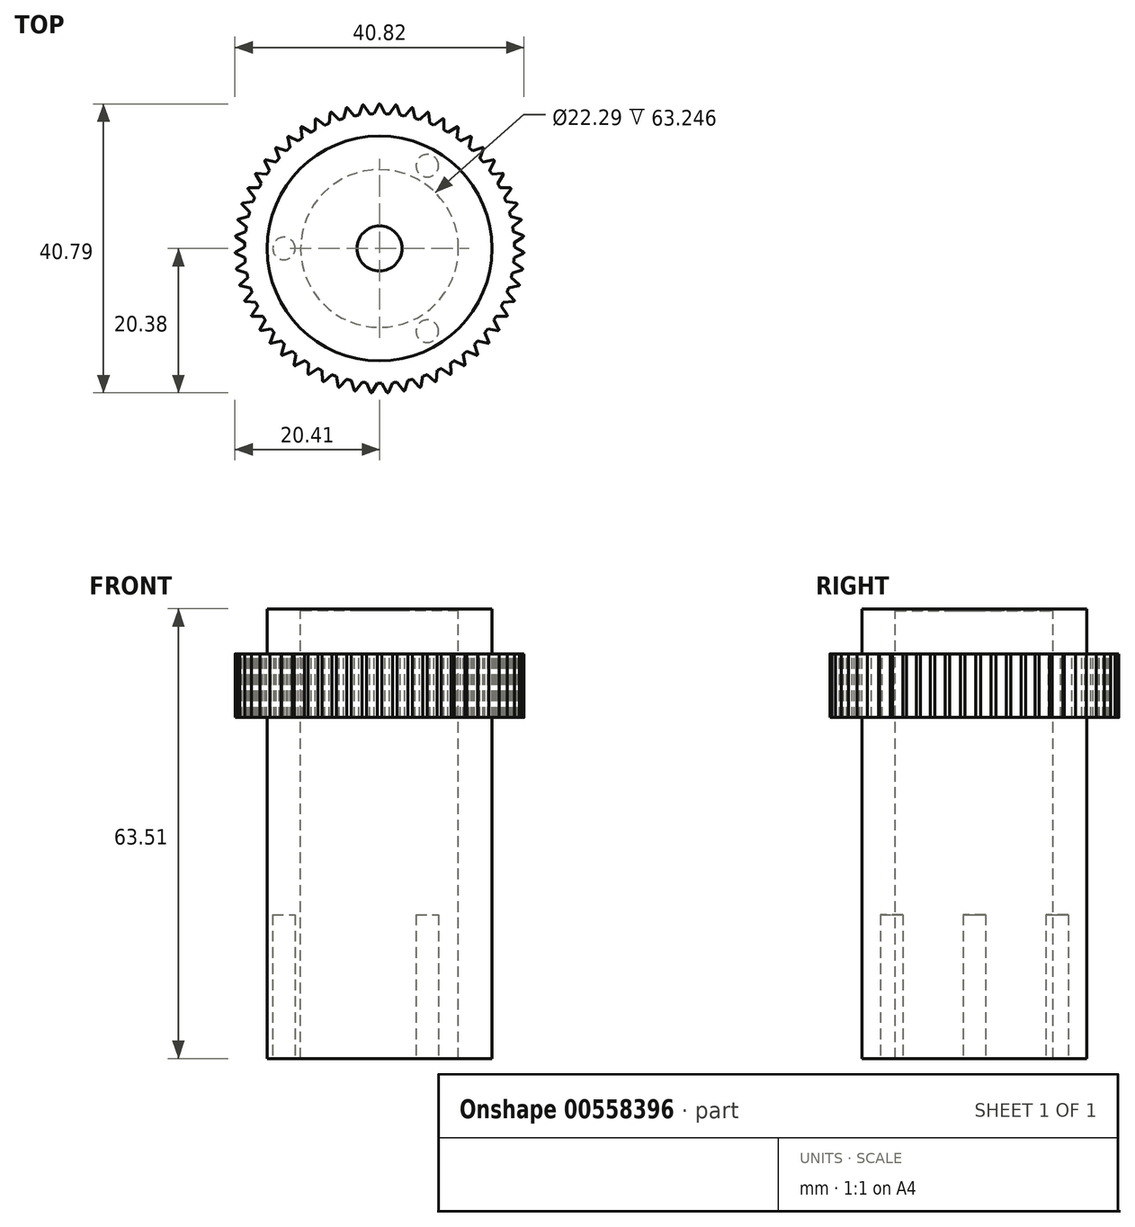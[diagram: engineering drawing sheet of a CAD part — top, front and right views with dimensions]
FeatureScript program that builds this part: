
annotation { "Feature Type Name" : "Feature", "Feature Type Description" : "" }
export const myFeature = defineFeature(function(context is Context, id is Id, definition is map)
    precondition{}
    {
        {
            var Q0;
            Q0=qCreatedBy(makeId("Front.planeOp"),FACE);
            var sketch = newSketch(context, id + "F0", { "sketchPlane" : qUnion([Q0])});
            skLineSegment(sketch, "E0.bottom", {"start": v(11.15, 34.92) * mm, "end": v(15.88, 34.92) * mm});
            skLineSegment(sketch, "E0.top", {"start": v(11.15, -28.58) * mm, "end": v(15.88, -28.58) * mm});
            skLineSegment(sketch, "E0.left", {"start": v(11.15, 34.92) * mm, "end": v(11.15, -28.58) * mm});
            skLineSegment(sketch, "E0.right", {"start": v(15.88, 34.92) * mm, "end": v(15.88, -28.58) * mm});
            skLineSegment(sketch, "E1", {"start": v(0, 43.43) * mm, "end": v(0, -51.55) * mm, "construction": true});
            skSolve(sketch);
        }
        {
            var Q0;
            Q0 = qSketchRegion(id + "F0", true);
            var Q1;
            Q1=sQuery(id+"F0.wireOp",EDGE,"E1");
            revolve(context, id + "F1", {"entities" : qUnion([Q0]), "axis" : qUnion([Q1]), "revolveType" : RevolveType.FULL});
        }
        {
            var Q0;
            Q0=makeQuery(id+"F1.opRevolve","SWEPT_FACE",FACE,{"disambiguationData":[OSD([sQuery(id+"F0.wireOp",EDGE,"E0.top")])]});
            var sketch = newSketch(context, id + "F2", { "sketchPlane" : qUnion([Q0])});
            skCircle(sketch, "E2", {"center": v(6.75, 11.69) * mm, "radius": 1.59 * mm});
            skCircle(sketch, "E3", {"center": v(6.75, -11.69) * mm, "radius": 1.59 * mm});
            skCircle(sketch, "E4", {"center": v(-13.5, 0) * mm, "radius": 1.59 * mm});
            skCircle(sketch, "E5", {"center": v(0, 0) * mm, "radius": 13.5 * mm});
            skLineSegment(sketch, "E6", {"start": v(0, 0) * mm, "end": v(-29.1, 0) * mm, "construction": true});
            skLineSegment(sketch, "E7", {"start": v(0, 0) * mm, "end": v(10.24, 17.73) * mm, "construction": true});
            skLineSegment(sketch, "E8", {"start": v(0, 0) * mm, "end": v(11.33, -19.63) * mm, "construction": true});
            skSolve(sketch);
        }
        {
            var Q0;
            {var subQ0=sQuery(id+"F2.wireOp",EDGE,"E5");var subQ1=sQuery(id+"F2.wireOp",EDGE,"E3");var subQ2=makeQuery(id+"F2.imprint","INTERSECT",VERTEX,{"disambiguationData":[OD(0.0)],"derivedFrom":[subQ1,subQ0]});Q0=makeQuery(id+"F2.imprint","IMPRINT",FACE,{"disambiguationData":[TD([[makeQuery(id+"F2.imprint","IMPRINT",EDGE,{"disambiguationData":[TD([[subQ2,-1.0]])],"derivedFrom":subQ1}),1.0]])]});}
            var Q1;
            {var subQ0=sQuery(id+"F2.wireOp",EDGE,"E5");var subQ1=sQuery(id+"F2.wireOp",EDGE,"E3");var subQ2=makeQuery(id+"F2.imprint","INTERSECT",VERTEX,{"disambiguationData":[OD(0.0)],"derivedFrom":[subQ1,subQ0]});Q1=makeQuery(id+"F2.imprint","IMPRINT",FACE,{"disambiguationData":[TD([[makeQuery(id+"F2.imprint","IMPRINT",EDGE,{"disambiguationData":[TD([[subQ2,1.0]])],"derivedFrom":subQ1}),1.0]])]});}
            var Q2;
            {var subQ0=sQuery(id+"F2.wireOp",EDGE,"E5");var subQ1=sQuery(id+"F2.wireOp",EDGE,"E2");var subQ2=makeQuery(id+"F2.imprint","INTERSECT",VERTEX,{"disambiguationData":[OD(0.0)],"derivedFrom":[subQ1,subQ0]});Q2=makeQuery(id+"F2.imprint","IMPRINT",FACE,{"disambiguationData":[TD([[makeQuery(id+"F2.imprint","IMPRINT",EDGE,{"disambiguationData":[TD([[subQ2,-1.0]])],"derivedFrom":subQ1}),1.0]])]});}
            var Q3;
            {var subQ0=sQuery(id+"F2.wireOp",EDGE,"E5");var subQ1=sQuery(id+"F2.wireOp",EDGE,"E2");var subQ2=makeQuery(id+"F2.imprint","INTERSECT",VERTEX,{"disambiguationData":[OD(0.0)],"derivedFrom":[subQ1,subQ0]});Q3=makeQuery(id+"F2.imprint","IMPRINT",FACE,{"disambiguationData":[TD([[makeQuery(id+"F2.imprint","IMPRINT",EDGE,{"disambiguationData":[TD([[subQ2,1.0]])],"derivedFrom":subQ1}),1.0]])]});}
            var Q4;
            {var subQ0=sQuery(id+"F2.wireOp",EDGE,"E5");var subQ1=sQuery(id+"F2.wireOp",EDGE,"E4");var subQ2=makeQuery(id+"F2.imprint","INTERSECT",VERTEX,{"disambiguationData":[OD(0.0)],"derivedFrom":[subQ1,subQ0]});Q4=makeQuery(id+"F2.imprint","IMPRINT",FACE,{"disambiguationData":[TD([[makeQuery(id+"F2.imprint","IMPRINT",EDGE,{"disambiguationData":[TD([[subQ2,-1.0]])],"derivedFrom":subQ1}),1.0]])]});}
            var Q5;
            {var subQ0=sQuery(id+"F2.wireOp",EDGE,"E5");var subQ1=sQuery(id+"F2.wireOp",EDGE,"E4");var subQ2=makeQuery(id+"F2.imprint","INTERSECT",VERTEX,{"disambiguationData":[OD(0.0)],"derivedFrom":[subQ1,subQ0]});Q5=makeQuery(id+"F2.imprint","IMPRINT",FACE,{"disambiguationData":[TD([[makeQuery(id+"F2.imprint","IMPRINT",EDGE,{"disambiguationData":[TD([[subQ2,1.0]])],"derivedFrom":subQ1}),1.0]])]});}
            extrude(context, id + "F3", {"entities" : qUnion([Q0, Q1, Q2, Q3, Q4, Q5]), "operationType" : NewBodyOperationType.REMOVE, "oppositeDirection" : true, "depth" : 20.32 * mm, "offsetDistance" : 25.4 * mm});
        }
        {
            var Q0;
            Q0=makeQuery(id+"F1.opRevolve","SWEPT_FACE",FACE,{"disambiguationData":[OSD([sQuery(id+"F0.wireOp",EDGE,"E0.bottom")])]});
            var sketch = newSketch(context, id + "F4", { "sketchPlane" : qUnion([Q0])});
            skCircle(sketch, "E9", {"center": v(0, 0) * mm, "radius": 3.18 * mm});
            skSolve(sketch);
        }
        {
            var Q0;
            Q0=makeQuery(id+"F4.imprint","IMPRINT",FACE,{"disambiguationData":[TD([[makeQuery(id+"F4.imprint","IMPRINT",EDGE,{"derivedFrom":sQuery(id+"F4.wireOp",EDGE,"E9")}),-1.0]])]});
            extrude(context, id + "F5", {"entities" : qUnion([Q0]), "operationType" : NewBodyOperationType.ADD, "oppositeDirection" : true, "depth" : 0.25 * mm, "offsetDistance" : 25.4 * mm});
        }
        {
            var Q0;
            {var subQ0=sQuery(id+"F0.wireOp",EDGE,"E0.bottom");Q0=makeQuery(id+"F5.boolean.opBoolean","MERGE",FACE,{"derivedFrom":[makeQuery(id+"F1.opRevolve","SWEPT_FACE",FACE,{"disambiguationData":[OSD([subQ0])]}),makeQuery(id+"F5.opExtrude","CAP_FACE",FACE,{"disambiguationData":[OSD([subQ0,sQuery(id+"F0.wireOp",EDGE,"E0.left"),sQuery(id+"F4.wireOp",EDGE,"E9")])],"isStart":true})]});}
            cPlane(context, id + "F6", {"entities" : qUnion([Q0]), "cplaneType" : CPlaneType.OFFSET, "offset" : 6.35 * mm, "oppositeDirection" : true, "width" : 152.4 * mm, "height" : 152.4 * mm});
        }
        {
            var Q0;
            Q0=qCreatedBy(id+"F6.planeOp",FACE);
            var sketch = newSketch(context, id + "F7", { "sketchPlane" : qUnion([Q0])});
            skCircle(sketch, "E10", {"center": v(0, 0) * mm, "radius": 19.05 * mm});
            skLineSegment(sketch, "E11", {"start": v(-0.76, 19.03) * mm, "end": v(-0.11, 20.34) * mm});
            skLineSegment(sketch, "E12", {"start": v(0.11, 20.34) * mm, "end": v(0.76, 19.03) * mm});
            skPoint(sketch, "E13.visualSharp", {"position": v(0, 20.57) * mm});
            skArc(sketch, "E14.filletArc", {"start": v(0.11, 20.34) * mm, "mid": v(0, 20.41) * mm, "end": v(-0.11, 20.34) * mm});
            skLineSegment(sketch, "E15.1.0", {"start": v(-2.2, 20.22) * mm, "end": v(-1.41, 19) * mm});
            skLineSegment(sketch, "E15.1.1", {"start": v(-2.93, 18.82) * mm, "end": v(-2.43, 20.2) * mm});
            skArc(sketch, "E15.1.2", {"start": v(-2.2, 20.22) * mm, "mid": v(-2.33, 20.28) * mm, "end": v(-2.43, 20.2) * mm});
            skLineSegment(sketch, "E15.2.0", {"start": v(-4.5, 19.84) * mm, "end": v(-3.57, 18.71) * mm});
            skLineSegment(sketch, "E15.2.1", {"start": v(-5.05, 18.37) * mm, "end": v(-4.72, 19.79) * mm});
            skArc(sketch, "E15.2.2", {"start": v(-4.5, 19.84) * mm, "mid": v(-4.62, 19.88) * mm, "end": v(-4.72, 19.79) * mm});
            skLineSegment(sketch, "E15.3.0", {"start": v(-6.73, 19.2) * mm, "end": v(-5.68, 18.18) * mm});
            skLineSegment(sketch, "E15.3.1", {"start": v(-7.11, 17.67) * mm, "end": v(-6.94, 19.12) * mm});
            skArc(sketch, "E15.3.2", {"start": v(-6.73, 19.2) * mm, "mid": v(-6.86, 19.23) * mm, "end": v(-6.94, 19.12) * mm});
            skLineSegment(sketch, "E15.4.0", {"start": v(-8.87, 18.3) * mm, "end": v(-7.71, 17.42) * mm});
            skLineSegment(sketch, "E15.4.1", {"start": v(-9.08, 16.75) * mm, "end": v(-9.08, 18.2) * mm});
            skArc(sketch, "E15.4.2", {"start": v(-8.87, 18.3) * mm, "mid": v(-9, 18.32) * mm, "end": v(-9.08, 18.2) * mm});
            skLineSegment(sketch, "E15.5.0", {"start": v(-10.9, 17.18) * mm, "end": v(-9.65, 16.43) * mm});
            skLineSegment(sketch, "E15.5.1", {"start": v(-10.93, 15.6) * mm, "end": v(-11.1, 17.05) * mm});
            skArc(sketch, "E15.5.2", {"start": v(-10.9, 17.18) * mm, "mid": v(-11.04, 17.17) * mm, "end": v(-11.1, 17.05) * mm});
            skLineSegment(sketch, "E15.6.0", {"start": v(-12.79, 15.82) * mm, "end": v(-11.46, 15.22) * mm});
            skLineSegment(sketch, "E15.6.1", {"start": v(-12.64, 14.25) * mm, "end": v(-12.97, 15.68) * mm});
            skArc(sketch, "E15.6.2", {"start": v(-12.79, 15.82) * mm, "mid": v(-12.92, 15.8) * mm, "end": v(-12.97, 15.68) * mm});
            skLineSegment(sketch, "E15.7.0", {"start": v(-14.51, 14.26) * mm, "end": v(-13.12, 13.81) * mm});
            skLineSegment(sketch, "E15.7.1", {"start": v(-14.18, 12.72) * mm, "end": v(-14.67, 14.1) * mm});
            skArc(sketch, "E15.7.2", {"start": v(-14.51, 14.26) * mm, "mid": v(-14.64, 14.23) * mm, "end": v(-14.67, 14.1) * mm});
            skLineSegment(sketch, "E15.8.0", {"start": v(-16.04, 12.51) * mm, "end": v(-14.6, 12.23) * mm});
            skLineSegment(sketch, "E15.8.1", {"start": v(-15.54, 11.02) * mm, "end": v(-16.18, 12.33) * mm});
            skArc(sketch, "E15.8.2", {"start": v(-16.04, 12.51) * mm, "mid": v(-16.17, 12.47) * mm, "end": v(-16.18, 12.33) * mm});
            skLineSegment(sketch, "E15.9.0", {"start": v(-17.36, 10.6) * mm, "end": v(-15.9, 10.48) * mm});
            skLineSegment(sketch, "E15.9.1", {"start": v(-16.7, 9.18) * mm, "end": v(-17.48, 10.4) * mm});
            skArc(sketch, "E15.9.2", {"start": v(-17.36, 10.6) * mm, "mid": v(-17.48, 10.54) * mm, "end": v(-17.48, 10.4) * mm});
            skLineSegment(sketch, "E15.10.0", {"start": v(-18.46, 8.55) * mm, "end": v(-17, 8.6) * mm});
            skLineSegment(sketch, "E15.10.1", {"start": v(-17.63, 7.21) * mm, "end": v(-18.55, 8.35) * mm});
            skArc(sketch, "E15.10.2", {"start": v(-18.46, 8.55) * mm, "mid": v(-18.57, 8.48) * mm, "end": v(-18.55, 8.35) * mm});
            skLineSegment(sketch, "E15.11.0", {"start": v(-19.31, 6.4) * mm, "end": v(-17.87, 6.6) * mm});
            skLineSegment(sketch, "E15.11.1", {"start": v(-18.34, 5.16) * mm, "end": v(-19.38, 6.18) * mm});
            skArc(sketch, "E15.11.2", {"start": v(-19.31, 6.4) * mm, "mid": v(-19.42, 6.3) * mm, "end": v(-19.38, 6.18) * mm});
            skLineSegment(sketch, "E15.12.0", {"start": v(-19.92, 4.15) * mm, "end": v(-18.5, 4.53) * mm});
            skLineSegment(sketch, "E15.12.1", {"start": v(-18.8, 3.03) * mm, "end": v(-19.96, 3.93) * mm});
            skArc(sketch, "E15.12.2", {"start": v(-19.92, 4.15) * mm, "mid": v(-20, 4.05) * mm, "end": v(-19.96, 3.93) * mm});
            skLineSegment(sketch, "E15.13.0", {"start": v(-20.26, 1.85) * mm, "end": v(-18.9, 2.39) * mm});
            skLineSegment(sketch, "E15.13.1", {"start": v(-19.03, 0.87) * mm, "end": v(-20.28, 1.63) * mm});
            skArc(sketch, "E15.13.2", {"start": v(-20.26, 1.85) * mm, "mid": v(-20.34, 1.75) * mm, "end": v(-20.28, 1.63) * mm});
            skLineSegment(sketch, "E15.14.0", {"start": v(-20.34, -0.47) * mm, "end": v(-19.05, 0.22) * mm});
            skLineSegment(sketch, "E15.14.1", {"start": v(-19, -1.3) * mm, "end": v(-20.33, -0.7) * mm});
            skArc(sketch, "E15.14.2", {"start": v(-20.34, -0.47) * mm, "mid": v(-20.4, -0.58) * mm, "end": v(-20.33, -0.7) * mm});
            skLineSegment(sketch, "E15.15.0", {"start": v(-20.15, -2.78) * mm, "end": v(-18.95, -1.95) * mm});
            skLineSegment(sketch, "E15.15.1", {"start": v(-18.73, -3.46) * mm, "end": v(-20.12, -3) * mm});
            skArc(sketch, "E15.15.2", {"start": v(-20.15, -2.78) * mm, "mid": v(-20.2, -2.9) * mm, "end": v(-20.12, -3) * mm});
            skLineSegment(sketch, "E15.16.0", {"start": v(-19.7, -5.06) * mm, "end": v(-18.6, -4.1) * mm});
            skLineSegment(sketch, "E15.16.1", {"start": v(-18.22, -5.58) * mm, "end": v(-19.65, -5.28) * mm});
            skArc(sketch, "E15.16.2", {"start": v(-19.7, -5.06) * mm, "mid": v(-19.74, -5.19) * mm, "end": v(-19.65, -5.28) * mm});
            skLineSegment(sketch, "E15.17.0", {"start": v(-19, -7.27) * mm, "end": v(-18.01, -6.2) * mm});
            skLineSegment(sketch, "E15.17.1", {"start": v(-17.46, -7.62) * mm, "end": v(-18.92, -7.49) * mm});
            skArc(sketch, "E15.17.2", {"start": v(-19, -7.27) * mm, "mid": v(-19.02, -7.4) * mm, "end": v(-18.92, -7.49) * mm});
            skLineSegment(sketch, "E15.18.0", {"start": v(-18.05, -9.4) * mm, "end": v(-17.2, -8.2) * mm});
            skLineSegment(sketch, "E15.18.1", {"start": v(-16.48, -9.56) * mm, "end": v(-17.94, -9.6) * mm});
            skArc(sketch, "E15.18.2", {"start": v(-18.05, -9.4) * mm, "mid": v(-18.06, -9.53) * mm, "end": v(-17.94, -9.6) * mm});
            skLineSegment(sketch, "E15.19.0", {"start": v(-16.86, -11.39) * mm, "end": v(-16.14, -10.12) * mm});
            skLineSegment(sketch, "E15.19.1", {"start": v(-15.28, -11.37) * mm, "end": v(-16.73, -11.58) * mm});
            skArc(sketch, "E15.19.2", {"start": v(-16.86, -11.39) * mm, "mid": v(-16.85, -11.52) * mm, "end": v(-16.73, -11.58) * mm});
            skLineSegment(sketch, "E15.20.0", {"start": v(-15.45, -13.24) * mm, "end": v(-14.88, -11.89) * mm});
            skLineSegment(sketch, "E15.20.1", {"start": v(-13.89, -13.04) * mm, "end": v(-15.3, -13.4) * mm});
            skArc(sketch, "E15.20.2", {"start": v(-15.45, -13.24) * mm, "mid": v(-15.43, -13.37) * mm, "end": v(-15.3, -13.4) * mm});
            skLineSegment(sketch, "E15.21.0", {"start": v(-13.84, -14.91) * mm, "end": v(-13.43, -13.5) * mm});
            skLineSegment(sketch, "E15.21.1", {"start": v(-12.3, -14.54) * mm, "end": v(-13.67, -15.07) * mm});
            skArc(sketch, "E15.21.2", {"start": v(-13.84, -14.91) * mm, "mid": v(-13.8, -15.04) * mm, "end": v(-13.67, -15.07) * mm});
            skLineSegment(sketch, "E15.22.0", {"start": v(-12.05, -16.4) * mm, "end": v(-11.8, -14.95) * mm});
            skLineSegment(sketch, "E15.22.1", {"start": v(-10.57, -15.85) * mm, "end": v(-11.87, -16.53) * mm});
            skArc(sketch, "E15.22.2", {"start": v(-12.05, -16.4) * mm, "mid": v(-12, -16.52) * mm, "end": v(-11.87, -16.53) * mm});
            skLineSegment(sketch, "E15.23.0", {"start": v(-10.1, -17.66) * mm, "end": v(-10.02, -16.2) * mm});
            skLineSegment(sketch, "E15.23.1", {"start": v(-8.7, -16.95) * mm, "end": v(-9.9, -17.77) * mm});
            skArc(sketch, "E15.23.2", {"start": v(-10.1, -17.66) * mm, "mid": v(-10.04, -17.78) * mm, "end": v(-9.9, -17.77) * mm});
            skLineSegment(sketch, "E15.24.0", {"start": v(-8.02, -18.7) * mm, "end": v(-8.11, -17.24) * mm});
            skLineSegment(sketch, "E15.24.1", {"start": v(-6.7, -17.83) * mm, "end": v(-7.81, -18.78) * mm});
            skArc(sketch, "E15.24.2", {"start": v(-8.02, -18.7) * mm, "mid": v(-7.95, -18.8) * mm, "end": v(-7.81, -18.78) * mm});
            skLineSegment(sketch, "E15.25.0", {"start": v(-5.84, -19.49) * mm, "end": v(-6.1, -18.05) * mm});
            skLineSegment(sketch, "E15.25.1", {"start": v(-4.63, -18.48) * mm, "end": v(-5.62, -19.55) * mm});
            skArc(sketch, "E15.25.2", {"start": v(-5.84, -19.49) * mm, "mid": v(-5.75, -19.59) * mm, "end": v(-5.62, -19.55) * mm});
            skLineSegment(sketch, "E15.26.0", {"start": v(-3.58, -20.03) * mm, "end": v(-4, -18.63) * mm});
            skLineSegment(sketch, "E15.26.1", {"start": v(-2.5, -18.89) * mm, "end": v(-3.36, -20.07) * mm});
            skArc(sketch, "E15.26.2", {"start": v(-3.58, -20.03) * mm, "mid": v(-3.48, -20.12) * mm, "end": v(-3.36, -20.07) * mm});
            skLineSegment(sketch, "E15.27.0", {"start": v(-1.28, -20.3) * mm, "end": v(-1.85, -18.96) * mm});
            skLineSegment(sketch, "E15.27.1", {"start": v(-0.33, -19.05) * mm, "end": v(-1.05, -20.32) * mm});
            skArc(sketch, "E15.27.2", {"start": v(-1.28, -20.3) * mm, "mid": v(-1.17, -20.38) * mm, "end": v(-1.05, -20.32) * mm});
            skLineSegment(sketch, "E15.28.0", {"start": v(1.05, -20.32) * mm, "end": v(0.33, -19.05) * mm});
            skLineSegment(sketch, "E15.28.1", {"start": v(1.85, -18.96) * mm, "end": v(1.28, -20.3) * mm});
            skArc(sketch, "E15.28.2", {"start": v(1.05, -20.32) * mm, "mid": v(1.17, -20.38) * mm, "end": v(1.28, -20.3) * mm});
            skLineSegment(sketch, "E15.29.0", {"start": v(3.36, -20.07) * mm, "end": v(2.5, -18.89) * mm});
            skLineSegment(sketch, "E15.29.1", {"start": v(4, -18.63) * mm, "end": v(3.58, -20.03) * mm});
            skArc(sketch, "E15.29.2", {"start": v(3.36, -20.07) * mm, "mid": v(3.48, -20.12) * mm, "end": v(3.58, -20.03) * mm});
            skLineSegment(sketch, "E16.3.30.0", {"start": v(6.1, -18.05) * mm, "end": v(5.84, -19.49) * mm});
            skLineSegment(sketch, "E16.5.30.0", {"start": v(5.62, -19.55) * mm, "end": v(4.63, -18.48) * mm});
            skArc(sketch, "E16.6.30.0", {"start": v(5.62, -19.55) * mm, "mid": v(5.75, -19.59) * mm, "end": v(5.84, -19.49) * mm});
            skLineSegment(sketch, "E16.3.31.0", {"start": v(8.11, -17.24) * mm, "end": v(8.02, -18.7) * mm});
            skLineSegment(sketch, "E16.5.31.0", {"start": v(7.81, -18.78) * mm, "end": v(6.7, -17.83) * mm});
            skArc(sketch, "E16.6.31.0", {"start": v(7.81, -18.78) * mm, "mid": v(7.95, -18.8) * mm, "end": v(8.02, -18.7) * mm});
            skLineSegment(sketch, "E16.3.32.0", {"start": v(10.02, -16.2) * mm, "end": v(10.1, -17.66) * mm});
            skLineSegment(sketch, "E16.5.32.0", {"start": v(9.9, -17.77) * mm, "end": v(8.7, -16.95) * mm});
            skArc(sketch, "E16.6.32.0", {"start": v(9.9, -17.77) * mm, "mid": v(10.04, -17.78) * mm, "end": v(10.1, -17.66) * mm});
            skLineSegment(sketch, "E16.3.33.0", {"start": v(11.8, -14.95) * mm, "end": v(12.05, -16.4) * mm});
            skLineSegment(sketch, "E16.5.33.0", {"start": v(11.87, -16.53) * mm, "end": v(10.57, -15.85) * mm});
            skArc(sketch, "E16.6.33.0", {"start": v(11.87, -16.53) * mm, "mid": v(12, -16.52) * mm, "end": v(12.05, -16.4) * mm});
            skLineSegment(sketch, "E16.3.34.0", {"start": v(13.43, -13.5) * mm, "end": v(13.84, -14.91) * mm});
            skLineSegment(sketch, "E16.5.34.0", {"start": v(13.67, -15.07) * mm, "end": v(12.3, -14.54) * mm});
            skArc(sketch, "E16.6.34.0", {"start": v(13.67, -15.07) * mm, "mid": v(13.8, -15.04) * mm, "end": v(13.84, -14.91) * mm});
            skLineSegment(sketch, "E16.3.35.0", {"start": v(14.88, -11.89) * mm, "end": v(15.45, -13.24) * mm});
            skLineSegment(sketch, "E16.5.35.0", {"start": v(15.3, -13.4) * mm, "end": v(13.89, -13.04) * mm});
            skArc(sketch, "E16.6.35.0", {"start": v(15.3, -13.4) * mm, "mid": v(15.43, -13.37) * mm, "end": v(15.45, -13.24) * mm});
            skLineSegment(sketch, "E16.3.36.0", {"start": v(16.14, -10.12) * mm, "end": v(16.86, -11.39) * mm});
            skLineSegment(sketch, "E16.5.36.0", {"start": v(16.73, -11.58) * mm, "end": v(15.28, -11.37) * mm});
            skArc(sketch, "E16.6.36.0", {"start": v(16.73, -11.58) * mm, "mid": v(16.85, -11.52) * mm, "end": v(16.86, -11.39) * mm});
            skLineSegment(sketch, "E16.3.37.0", {"start": v(17.2, -8.2) * mm, "end": v(18.05, -9.4) * mm});
            skLineSegment(sketch, "E16.5.37.0", {"start": v(17.94, -9.6) * mm, "end": v(16.48, -9.56) * mm});
            skArc(sketch, "E16.6.37.0", {"start": v(17.94, -9.6) * mm, "mid": v(18.06, -9.53) * mm, "end": v(18.05, -9.4) * mm});
            skLineSegment(sketch, "E16.3.38.0", {"start": v(18.01, -6.2) * mm, "end": v(19, -7.27) * mm});
            skLineSegment(sketch, "E16.5.38.0", {"start": v(18.92, -7.49) * mm, "end": v(17.46, -7.62) * mm});
            skArc(sketch, "E16.6.38.0", {"start": v(18.92, -7.49) * mm, "mid": v(19.02, -7.4) * mm, "end": v(19, -7.27) * mm});
            skLineSegment(sketch, "E16.3.39.0", {"start": v(18.6, -4.1) * mm, "end": v(19.7, -5.06) * mm});
            skLineSegment(sketch, "E16.5.39.0", {"start": v(19.65, -5.28) * mm, "end": v(18.22, -5.58) * mm});
            skArc(sketch, "E16.6.39.0", {"start": v(19.65, -5.28) * mm, "mid": v(19.74, -5.19) * mm, "end": v(19.7, -5.06) * mm});
            skLineSegment(sketch, "E16.3.40.0", {"start": v(18.95, -1.95) * mm, "end": v(20.15, -2.78) * mm});
            skLineSegment(sketch, "E16.5.40.0", {"start": v(20.12, -3) * mm, "end": v(18.73, -3.46) * mm});
            skArc(sketch, "E16.6.40.0", {"start": v(20.12, -3) * mm, "mid": v(20.2, -2.9) * mm, "end": v(20.15, -2.78) * mm});
            skLineSegment(sketch, "E16.3.41.0", {"start": v(19.05, 0.22) * mm, "end": v(20.34, -0.47) * mm});
            skLineSegment(sketch, "E16.5.41.0", {"start": v(20.33, -0.7) * mm, "end": v(19, -1.3) * mm});
            skArc(sketch, "E16.6.41.0", {"start": v(20.33, -0.7) * mm, "mid": v(20.4, -0.58) * mm, "end": v(20.34, -0.47) * mm});
            skLineSegment(sketch, "E16.3.42.0", {"start": v(18.9, 2.39) * mm, "end": v(20.26, 1.85) * mm});
            skLineSegment(sketch, "E16.5.42.0", {"start": v(20.28, 1.63) * mm, "end": v(19.03, 0.87) * mm});
            skArc(sketch, "E16.6.42.0", {"start": v(20.28, 1.63) * mm, "mid": v(20.34, 1.75) * mm, "end": v(20.26, 1.85) * mm});
            skLineSegment(sketch, "E16.3.43.0", {"start": v(18.5, 4.53) * mm, "end": v(19.92, 4.15) * mm});
            skLineSegment(sketch, "E16.5.43.0", {"start": v(19.96, 3.93) * mm, "end": v(18.8, 3.03) * mm});
            skArc(sketch, "E16.6.43.0", {"start": v(19.96, 3.93) * mm, "mid": v(20, 4.05) * mm, "end": v(19.92, 4.15) * mm});
            skLineSegment(sketch, "E16.3.44.0", {"start": v(17.87, 6.6) * mm, "end": v(19.31, 6.4) * mm});
            skLineSegment(sketch, "E16.5.44.0", {"start": v(19.38, 6.18) * mm, "end": v(18.34, 5.16) * mm});
            skArc(sketch, "E16.6.44.0", {"start": v(19.38, 6.18) * mm, "mid": v(19.42, 6.3) * mm, "end": v(19.31, 6.4) * mm});
            skLineSegment(sketch, "E16.3.45.0", {"start": v(17, 8.6) * mm, "end": v(18.46, 8.55) * mm});
            skLineSegment(sketch, "E16.5.45.0", {"start": v(18.55, 8.35) * mm, "end": v(17.63, 7.21) * mm});
            skArc(sketch, "E16.6.45.0", {"start": v(18.55, 8.35) * mm, "mid": v(18.57, 8.48) * mm, "end": v(18.46, 8.55) * mm});
            skLineSegment(sketch, "E16.3.46.0", {"start": v(15.9, 10.48) * mm, "end": v(17.36, 10.6) * mm});
            skLineSegment(sketch, "E16.5.46.0", {"start": v(17.48, 10.4) * mm, "end": v(16.7, 9.18) * mm});
            skArc(sketch, "E16.6.46.0", {"start": v(17.48, 10.4) * mm, "mid": v(17.48, 10.54) * mm, "end": v(17.36, 10.6) * mm});
            skLineSegment(sketch, "E16.3.47.0", {"start": v(14.6, 12.23) * mm, "end": v(16.04, 12.51) * mm});
            skLineSegment(sketch, "E16.5.47.0", {"start": v(16.18, 12.33) * mm, "end": v(15.54, 11.02) * mm});
            skArc(sketch, "E16.6.47.0", {"start": v(16.18, 12.33) * mm, "mid": v(16.17, 12.47) * mm, "end": v(16.04, 12.51) * mm});
            skLineSegment(sketch, "E16.3.48.0", {"start": v(13.12, 13.81) * mm, "end": v(14.51, 14.26) * mm});
            skLineSegment(sketch, "E16.5.48.0", {"start": v(14.67, 14.1) * mm, "end": v(14.18, 12.72) * mm});
            skArc(sketch, "E16.6.48.0", {"start": v(14.67, 14.1) * mm, "mid": v(14.64, 14.23) * mm, "end": v(14.51, 14.26) * mm});
            skLineSegment(sketch, "E16.3.49.0", {"start": v(11.46, 15.22) * mm, "end": v(12.79, 15.82) * mm});
            skLineSegment(sketch, "E16.5.49.0", {"start": v(12.97, 15.68) * mm, "end": v(12.64, 14.25) * mm});
            skArc(sketch, "E16.6.49.0", {"start": v(12.97, 15.68) * mm, "mid": v(12.92, 15.8) * mm, "end": v(12.79, 15.82) * mm});
            skLineSegment(sketch, "E16.3.50.0", {"start": v(9.65, 16.43) * mm, "end": v(10.9, 17.18) * mm});
            skLineSegment(sketch, "E16.5.50.0", {"start": v(11.1, 17.05) * mm, "end": v(10.93, 15.6) * mm});
            skArc(sketch, "E16.6.50.0", {"start": v(11.1, 17.05) * mm, "mid": v(11.04, 17.17) * mm, "end": v(10.9, 17.18) * mm});
            skLineSegment(sketch, "E16.3.51.0", {"start": v(7.71, 17.42) * mm, "end": v(8.87, 18.3) * mm});
            skLineSegment(sketch, "E16.5.51.0", {"start": v(9.08, 18.2) * mm, "end": v(9.08, 16.75) * mm});
            skArc(sketch, "E16.6.51.0", {"start": v(9.08, 18.2) * mm, "mid": v(9, 18.32) * mm, "end": v(8.87, 18.3) * mm});
            skLineSegment(sketch, "E16.3.52.0", {"start": v(5.68, 18.18) * mm, "end": v(6.73, 19.2) * mm});
            skLineSegment(sketch, "E16.5.52.0", {"start": v(6.94, 19.12) * mm, "end": v(7.11, 17.67) * mm});
            skArc(sketch, "E16.6.52.0", {"start": v(6.94, 19.12) * mm, "mid": v(6.86, 19.23) * mm, "end": v(6.73, 19.2) * mm});
            skLineSegment(sketch, "E16.3.53.0", {"start": v(3.57, 18.71) * mm, "end": v(4.5, 19.84) * mm});
            skLineSegment(sketch, "E16.5.53.0", {"start": v(4.72, 19.79) * mm, "end": v(5.05, 18.37) * mm});
            skArc(sketch, "E16.6.53.0", {"start": v(4.72, 19.79) * mm, "mid": v(4.62, 19.88) * mm, "end": v(4.5, 19.84) * mm});
            skLineSegment(sketch, "E16.3.54.0", {"start": v(1.41, 19) * mm, "end": v(2.2, 20.22) * mm});
            skLineSegment(sketch, "E16.5.54.0", {"start": v(2.43, 20.2) * mm, "end": v(2.93, 18.82) * mm});
            skArc(sketch, "E16.6.54.0", {"start": v(2.43, 20.2) * mm, "mid": v(2.33, 20.28) * mm, "end": v(2.2, 20.22) * mm});
            skSolve(sketch);
        }
        {
            var Q0;
            Q0 = qSketchRegion(id + "F7", true);
            extrude(context, id + "F8", {"entities" : qUnion([Q0]), "operationType" : NewBodyOperationType.ADD, "oppositeDirection" : true, "depth" : 9 * mm, "offsetDistance" : 25.4 * mm});
        }
        {
            var Q0;
            Q0=makeQuery(id+"F1.opRevolve","SWEPT_FACE",FACE,{"disambiguationData":[OSD([sQuery(id+"F0.wireOp",EDGE,"E0.top")])]});
            var sketch = newSketch(context, id + "F9", { "sketchPlane" : qUnion([Q0])});
            skCircle(sketch, "E17", {"center": v(0, 0) * mm, "radius": 11.15 * mm});
            skSolve(sketch);
        }
        {
            var Q0;
            Q0 = qSketchRegion(id + "F9", true);
            extrude(context, id + "F10", {"entities" : qUnion([Q0]), "operationType" : NewBodyOperationType.REMOVE, "oppositeDirection" : true, "depth" : 60.96 * mm, "offsetDistance" : 25.4 * mm});
        }
    });
